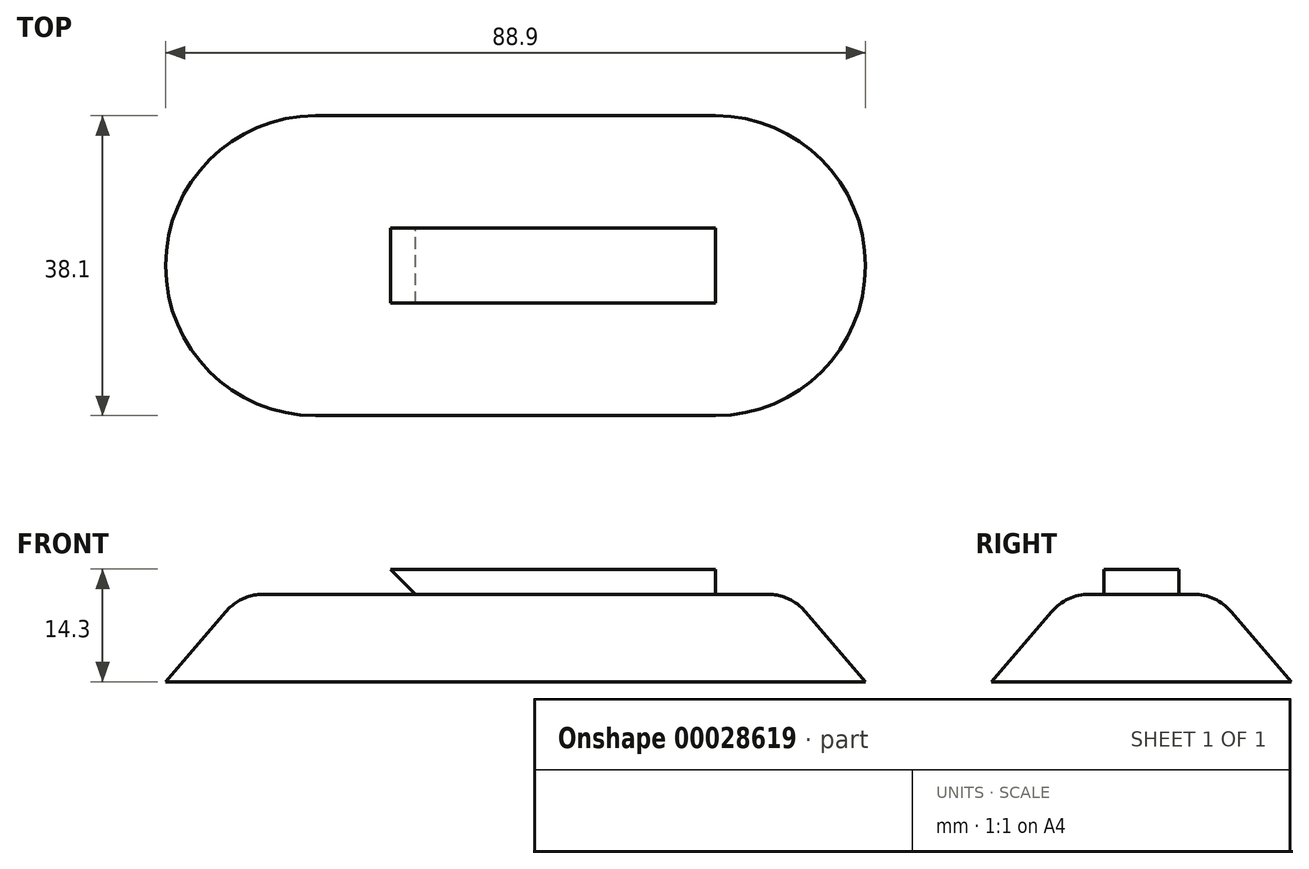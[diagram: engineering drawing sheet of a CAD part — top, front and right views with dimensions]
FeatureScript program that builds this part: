
annotation { "Feature Type Name" : "Feature", "Feature Type Description" : "" }
export const myFeature = defineFeature(function(context is Context, id is Id, definition is map)
    precondition{}
    {
        {
            var Q0;
            Q0=qCreatedBy(makeId("Top.planeOp"),FACE);
            var sketch = newSketch(context, id + "F0", { "sketchPlane" : qUnion([Q0])});
            skArc(sketch, "E0", {"start": v(0, 19.05) * mm, "mid": v(-19.05, 0) * mm, "end": v(0, -19.05) * mm});
            skLineSegment(sketch, "E1", {"start": v(0, -19.05) * mm, "end": v(0, 19.05) * mm, "construction": true});
            skLineSegment(sketch, "E2", {"start": v(0, 19.05) * mm, "end": v(50.8, 19.05) * mm});
            skLineSegment(sketch, "E3", {"start": v(0, -19.05) * mm, "end": v(50.8, -19.05) * mm});
            skLineSegment(sketch, "E4", {"start": v(50.8, 19.05) * mm, "end": v(50.8, -19.05) * mm});
            skSolve(sketch);
        }
        {
            var Q0;
            Q0=qCreatedBy(makeId("Top.planeOp"),FACE);
            cPlane(context, id + "F1", {"entities" : qUnion([Q0]), "cplaneType" : CPlaneType.OFFSET, "offset" : 11.1 * mm, "width" : 152.4 * mm, "height" : 152.4 * mm});
        }
        {
            var Q0;
            Q0=qCreatedBy(id+"F1.planeOp",FACE);
            var sketch = newSketch(context, id + "F2", { "sketchPlane" : qUnion([Q0])});
            skArc(sketch, "E5", {"start": v(0, 9.53) * mm, "mid": v(-9.53, 0) * mm, "end": v(0, -9.53) * mm});
            skLineSegment(sketch, "E6", {"start": v(0, 9.53) * mm, "end": v(50.8, 9.53) * mm});
            skLineSegment(sketch, "E7", {"start": v(0, -9.53) * mm, "end": v(50.8, -9.52) * mm});
            skLineSegment(sketch, "E8.0", {"start": v(50.8, 9.53) * mm, "end": v(50.8, -9.52) * mm, "construction": true});
            skLineSegment(sketch, "E9", {"start": v(50.8, 9.53) * mm, "end": v(50.8, -9.52) * mm});
            skSolve(sketch);
        }
        {
            var Q0;
            Q0=makeQuery(id+"F0.imprint","IMPRINT",FACE,{"disambiguationData":[TD([[makeQuery(id+"F0.imprint","IMPRINT",EDGE,{"derivedFrom":sQuery(id+"F0.wireOp",EDGE,"E0")}),1.0]])]});
            var Q1;
            Q1=makeQuery(id+"F2.imprint","IMPRINT",FACE,{"disambiguationData":[TD([[makeQuery(id+"F2.imprint","IMPRINT",EDGE,{"derivedFrom":sQuery(id+"F2.wireOp",EDGE,"E5")}),1.0]])]});
            loft(context, id + "F3", {"sheetProfilesArray" : [{ "sheetProfileEntities" : qUnion([Q0]) }, { "sheetProfileEntities" : qUnion([Q1]) }]});
        }
        {
            var Q0;
            Q0=qCreatedBy(makeId("Front.planeOp"),FACE);
            var sketch = newSketch(context, id + "F4", { "sketchPlane" : qUnion([Q0])});
            skLineSegment(sketch, "E10.0", {"start": v(0, 11.11) * mm, "end": v(50.8, 11.11) * mm, "construction": true});
            skLineSegment(sketch, "E11", {"start": v(12.7, 11.11) * mm, "end": v(9.52, 14.3) * mm});
            skLineSegment(sketch, "E12", {"start": v(9.52, 14.3) * mm, "end": v(50.8, 14.3) * mm});
            skLineSegment(sketch, "E13", {"start": v(50.8, 11.11) * mm, "end": v(50.8, 14.3) * mm});
            skLineSegment(sketch, "E14", {"start": v(12.7, 11.11) * mm, "end": v(50.8, 11.11) * mm});
            skSolve(sketch);
        }
        {
            var Q0;
            Q0 = qSketchRegion(id + "F4", true);
            extrude(context, id + "F5", {"entities" : qUnion([Q0]), "operationType" : NewBodyOperationType.ADD, "endBound" : BoundingType.SYMMETRIC, "depth" : 9.52 * mm});
        }
        {
            var Q0;
            Q0=makeQuery(id+"F3.opLoft","MID_CAP_EDGE",EDGE,{"disambiguationData":[OSD([sQuery(id+"F2.wireOp",EDGE,"E5"),sQuery(id+"F2.wireOp",EDGE,"E7"),sQuery(id+"F2.wireOp",EDGE,"E9")])],"capPos":1.0});
            fillet(context, id + "F6", {"entities" : qUnion([Q0]), "radius" : 6.35 * mm, "tangentPropagation" : true, "allowEdgeOverflow" : false});
        }
        {
            var Q0;
            Q0=makeQuery(id+"F5.boolean.opBoolean","MERGE",FACE,{"derivedFrom":[makeQuery(id+"F3.opLoft","SWEPT_FACE",FACE,{"disambiguationData":[OSD([sQuery(id+"F0.wireOp",EDGE,"E2"),sQuery(id+"F0.wireOp",EDGE,"E3"),sQuery(id+"F0.wireOp",EDGE,"E4"),sQuery(id+"F2.wireOp",EDGE,"E6"),sQuery(id+"F2.wireOp",EDGE,"E7"),sQuery(id+"F2.wireOp",EDGE,"E9")])]}),makeQuery(id+"F5.opExtrude","SWEPT_FACE",FACE,{"disambiguationData":[OSD([sQuery(id+"F4.wireOp",EDGE,"E13")])]})]});
            var sketch = newSketch(context, id + "F7", { "sketchPlane" : qUnion([Q0])});
            skLineSegment(sketch, "E15.0", {"start": v(-6.6, 11.11) * mm, "end": v(-4.76, 11.11) * mm});
            skArc(sketch, "E15.1", {"start": v(-6.6, 11.11) * mm, "mid": v(-9.26, 10.53) * mm, "end": v(-11.43, 8.9) * mm});
            skLineSegment(sketch, "E15.2", {"start": v(-19.05, 0) * mm, "end": v(-11.43, 8.9) * mm});
            skLineSegment(sketch, "E16", {"start": v(-4.76, 11.11) * mm, "end": v(0, 11.11) * mm});
            skLineSegment(sketch, "E17", {"start": v(0, 0) * mm, "end": v(0, 11.11) * mm, "construction": true});
            skLineSegment(sketch, "E18", {"start": v(-19.05, 0) * mm, "end": v(0, 0) * mm});
            skLineSegment(sketch, "E19", {"start": v(0, 11.11) * mm, "end": v(0, 0) * mm});
            skSolve(sketch);
        }
        {
            var Q0;
            Q0 = qSketchRegion(id + "F7", true);
            var Q1;
            Q1=sQuery(id+"F7.wireOp",EDGE,"E19");
            revolve(context, id + "F8", {"operationType" : NewBodyOperationType.ADD, "entities" : qUnion([Q0]), "axis" : qUnion([Q1]), "revolveType" : RevolveType.ONE_DIRECTION, "oppositeDirection" : true, "angle" : 180 * degree});
        }
    });
